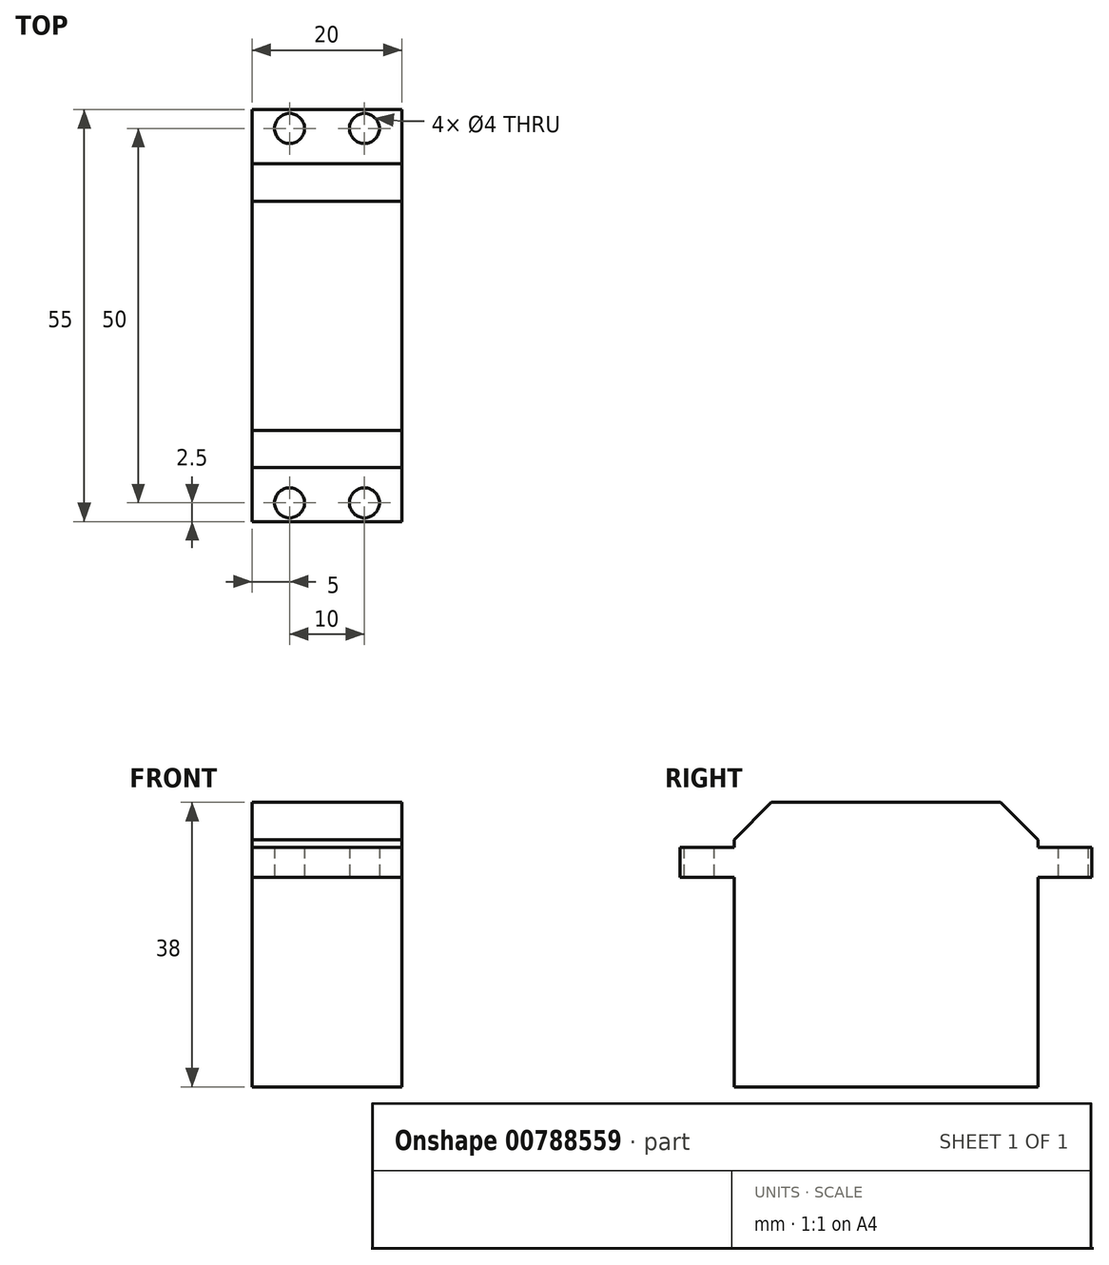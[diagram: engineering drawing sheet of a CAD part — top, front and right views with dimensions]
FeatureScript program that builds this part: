
annotation { "Feature Type Name" : "Feature", "Feature Type Description" : "" }
export const myFeature = defineFeature(function(context is Context, id is Id, definition is map)
    precondition{}
    {
        {
            var Q0;
            Q0=qCreatedBy(makeId("Right.planeOp"),FACE);
            var sketch = newSketch(context, id + "F0", { "sketchPlane" : qUnion([Q0])});
            skLineSegment(sketch, "E0.bottom", {"start": v(20.3, -20.16) * mm, "end": v(-20.3, -20.16) * mm});
            skLineSegment(sketch, "E0.top", {"start": v(20.3, 17.84) * mm, "end": v(-20.3, 17.84) * mm});
            skLineSegment(sketch, "E0.left", {"start": v(20.3, -20.16) * mm, "end": v(20.3, 17.84) * mm});
            skLineSegment(sketch, "E0.right", {"start": v(-20.3, -20.16) * mm, "end": v(-20.3, 17.84) * mm});
            skLineSegment(sketch, "E1.bottom", {"start": v(-27.5, 11.84) * mm, "end": v(27.5, 11.84) * mm});
            skLineSegment(sketch, "E1.top", {"start": v(-27.5, 7.84) * mm, "end": v(27.5, 7.84) * mm});
            skLineSegment(sketch, "E1.left", {"start": v(-27.5, 11.84) * mm, "end": v(-27.5, 7.84) * mm});
            skLineSegment(sketch, "E1.right", {"start": v(27.5, 11.84) * mm, "end": v(27.5, 7.84) * mm});
            skPoint(sketch, "E1.middle", {"position": v(0, 9.84) * mm});
            skSolve(sketch);
        }
        {
            var Q0;
            {var subQ5=sQuery(id+"F0.wireOp",EDGE,"E1.right");Q0=makeQuery(id+"F0.imprint","IMPRINT",FACE,{"disambiguationData":[TD([[makeQuery(id+"F0.imprint","IMPRINT",EDGE,{"derivedFrom":subQ5}),-1.0]])]});}
            var Q1;
            {var subQ0=sQuery(id+"F0.wireOp",EDGE,"E0.top");Q1=makeQuery(id+"F0.imprint","IMPRINT",FACE,{"disambiguationData":[TD([[makeQuery(id+"F0.imprint","IMPRINT",EDGE,{"derivedFrom":subQ0}),1.0]])]});}
            var Q2;
            {var subQ0=sQuery(id+"F0.wireOp",EDGE,"E0.bottom");Q2=makeQuery(id+"F0.imprint","IMPRINT",FACE,{"disambiguationData":[TD([[makeQuery(id+"F0.imprint","IMPRINT",EDGE,{"derivedFrom":subQ0}),-1.0]])]});}
            var Q3;
            {var subQ5=sQuery(id+"F0.wireOp",EDGE,"E1.left");Q3=makeQuery(id+"F0.imprint","IMPRINT",FACE,{"disambiguationData":[TD([[makeQuery(id+"F0.imprint","IMPRINT",EDGE,{"derivedFrom":subQ5}),1.0]])]});}
            var Q4;
            {var subQ0=sQuery(id+"F0.wireOp",EDGE,"E1.top");var subQ1=sQuery(id+"F0.wireOp",EDGE,"E0.left");var subQ2=makeQuery(id+"F0.imprint","INTERSECT",VERTEX,{"derivedFrom":[subQ1,subQ0]});Q4=makeQuery(id+"F0.imprint","IMPRINT",FACE,{"disambiguationData":[TD([[makeQuery(id+"F0.imprint","IMPRINT",EDGE,{"disambiguationData":[TD([[subQ2,-1.0]])],"derivedFrom":subQ1}),1.0]])]});}
            extrude(context, id + "F1", {"entities" : qUnion([Q0, Q1, Q2, Q3, Q4]), "endBound" : BoundingType.SYMMETRIC, "depth" : 20 * mm, "offsetDistance" : 25 * mm});
        }
        {
            var Q0;
            Q0=qCreatedBy(makeId("Top.planeOp"),FACE);
            var sketch = newSketch(context, id + "F2", { "sketchPlane" : qUnion([Q0])});
            skLineSegment(sketch, "E2.bottom", {"start": v(-5, 25) * mm, "end": v(5, 25) * mm, "construction": true});
            skLineSegment(sketch, "E2.top", {"start": v(-5, -25) * mm, "end": v(5, -25) * mm, "construction": true});
            skLineSegment(sketch, "E2.left", {"start": v(-5, 25) * mm, "end": v(-5, -25) * mm, "construction": true});
            skLineSegment(sketch, "E2.right", {"start": v(5, 25) * mm, "end": v(5, -25) * mm, "construction": true});
            skPoint(sketch, "E2.middle", {"position": v(0, 0) * mm});
            skPoint(sketch, "E3", {"position": v(-5, 25) * mm});
            skPoint(sketch, "E4", {"position": v(5, 25) * mm});
            skPoint(sketch, "E5", {"position": v(5, -25) * mm});
            skPoint(sketch, "E6", {"position": v(-5, -25) * mm});
            skCircle(sketch, "E7", {"center": v(-0.1, -8.3) * mm, "radius": 2.5 * mm});
            skSolve(sketch);
        }
        {
            var Q0;
            Q0=sQuery(id+"F2.wireOp",VERTEX,"E3");
            var Q1;
            Q1=sQuery(id+"F2.wireOp",VERTEX,"E4");
            var Q2;
            Q2=sQuery(id+"F2.wireOp",VERTEX,"E5");
            var Q3;
            Q3=sQuery(id+"F2.wireOp",VERTEX,"E6");
            var Q4;
            Q4=makeQuery(id+"F1.opExtrude","SWEPT_BODY",BODY,{"disambiguationData":[OSD([sQuery(id+"F0.wireOp",EDGE,"E0.bottom"),sQuery(id+"F0.wireOp",EDGE,"E0.top"),sQuery(id+"F0.wireOp",EDGE,"E0.left"),sQuery(id+"F0.wireOp",EDGE,"E0.right"),sQuery(id+"F0.wireOp",EDGE,"E1.bottom"),sQuery(id+"F0.wireOp",EDGE,"E1.top"),sQuery(id+"F0.wireOp",EDGE,"E1.left"),sQuery(id+"F0.wireOp",EDGE,"E1.right")])]});
            hole(context, id + "F3", {"style" : HoleStyle.SIMPLE, "endStyle" : HoleEndStyle.THROUGH, "oppositeDirection" : true, "holeDiameter" : 4 * mm, "majorDiameter" : 5 * mm, "isTappedThrough" : true, "tappedDepth" : 12 * mm, "tapClearance" : 3, "locations" : qUnion([Q0, Q1, Q2, Q3]), "scope" : qUnion([Q4])});
        }
        {
            var Q0;
            Q0=makeQuery(id+"F1.opExtrude","SWEPT_EDGE",EDGE,{"disambiguationData":[OSD([sQuery(id+"F0.wireOp",EDGE,"E0.top"),sQuery(id+"F0.wireOp",EDGE,"E0.right")])]});
            var Q1;
            Q1=makeQuery(id+"F1.opExtrude","SWEPT_EDGE",EDGE,{"disambiguationData":[OSD([sQuery(id+"F0.wireOp",EDGE,"E0.top"),sQuery(id+"F0.wireOp",EDGE,"E0.left")])]});
            chamfer(context, id + "F4", {"entities" : qUnion([Q0, Q1]), "width" : 5 * mm, "tangentPropagation" : true});
        }
        {
            var Q0;
            Q0=sQuery(id+"F2.wireOp",EDGE,"E7");
            extrude(context, id + "F5", {"bodyType" : ToolBodyType.SURFACE, "surfaceEntities" : qUnion([Q0]), "depth" : 25 * mm, "offsetDistance" : 25 * mm});
        }
    });
